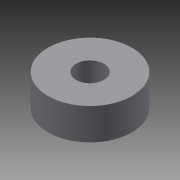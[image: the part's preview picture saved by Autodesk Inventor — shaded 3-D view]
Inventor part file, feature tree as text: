
AUTODESK INVENTOR PART (.ipt)
format: ipt  version: 2013 (Build 170138000, 138)  size: 72,192 bytes
history: native  units: in
note: dims shown in document units (in); Inventor stores cm internally (conversion verified against a paired STEP export)
features: extrude x1, sketch x1
ambient origin geometry x8: Origin, YZ Plane, XZ Plane, XY Plane, X Axis, Y Axis, Z Axis, Center Point
bodies: Solid1 (feature_tree)
feature tree (2):
  extrude  "Extrusion1"  Depth=0.75in
  sketch  "Sketch1"  dims[d0=0.25in d1=0.75in d2=0.2812in d3=0.0in]
